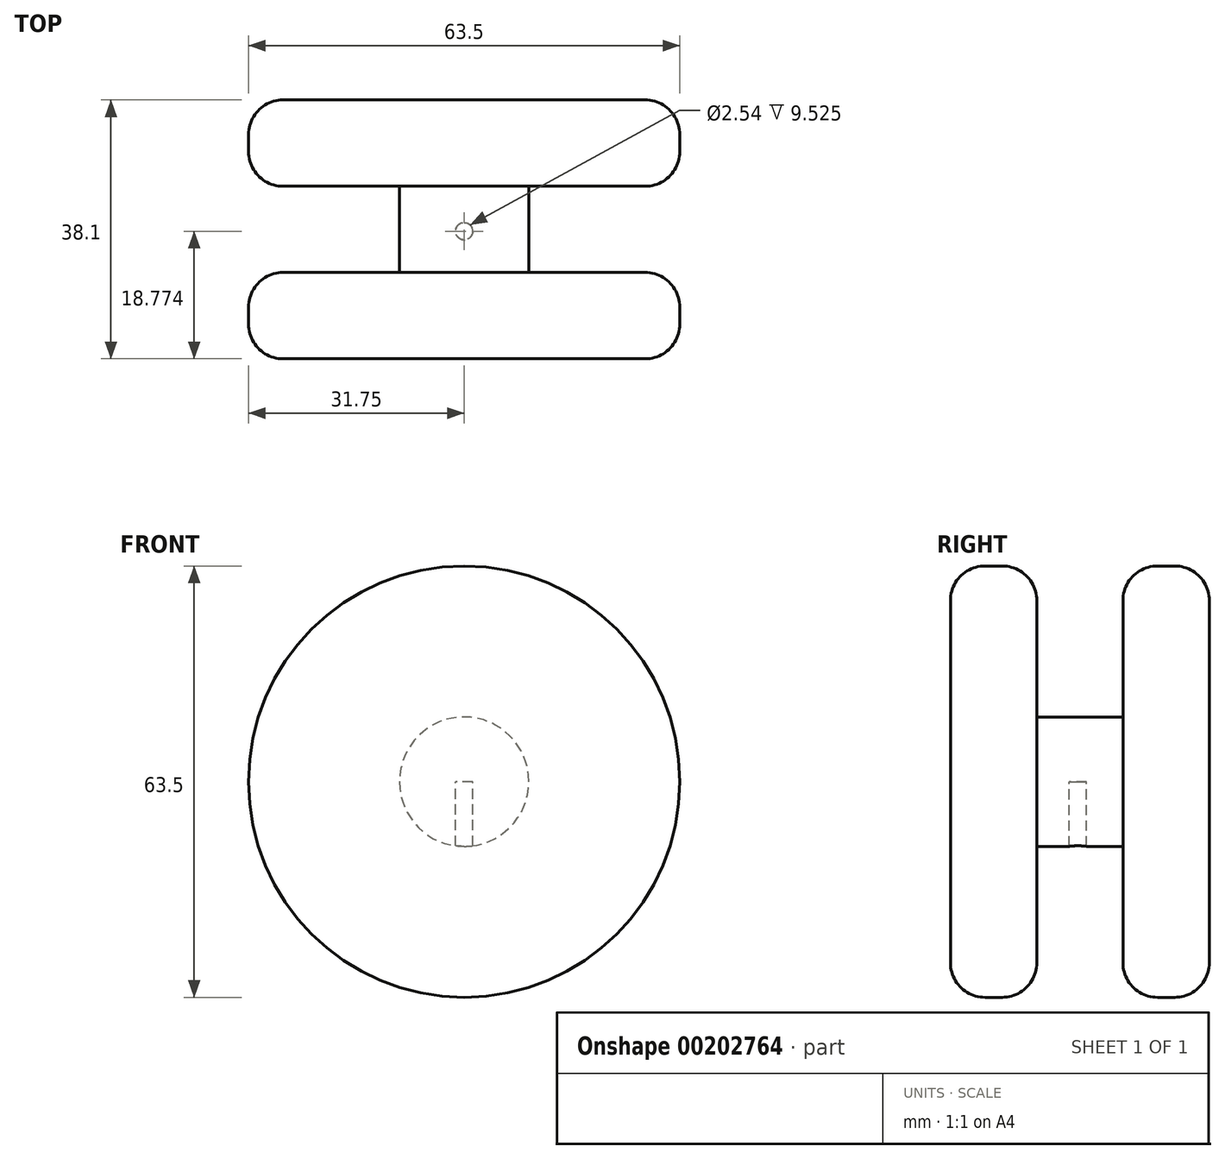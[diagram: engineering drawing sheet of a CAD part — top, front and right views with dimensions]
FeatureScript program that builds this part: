
annotation { "Feature Type Name" : "Feature", "Feature Type Description" : "" }
export const myFeature = defineFeature(function(context is Context, id is Id, definition is map)
    precondition{}
    {
        {
            var Q0;
            Q0=qCreatedBy(makeId("Front.planeOp"),FACE);
            var sketch = newSketch(context, id + "F0", { "sketchPlane" : qUnion([Q0])});
            skCircle(sketch, "E0", {"center": v(0, 0) * mm, "radius": 31.75 * mm});
            skSolve(sketch);
        }
        {
            var Q0;
            Q0=makeQuery(id+"F0.imprint","IMPRINT",FACE,{"disambiguationData":[TD([[makeQuery(id+"F0.imprint","IMPRINT",EDGE,{"derivedFrom":sQuery(id+"F0.wireOp",EDGE,"E0")}),1.0]])]});
            extrude(context, id + "F1", {"entities" : qUnion([Q0]), "depth" : 12.7 * mm});
        }
        {
            var Q0;
            Q0=makeQuery(id+"F1.opExtrude","CAP_FACE",FACE,{"disambiguationData":[OSD([sQuery(id+"F0.wireOp",EDGE,"E0")])],"isStart":false});
            var Q1;
            Q1=makeQuery(id+"F1.opExtrude","CAP_FACE",FACE,{"disambiguationData":[OSD([sQuery(id+"F0.wireOp",EDGE,"E0")])],"isStart":true});
            fillet(context, id + "F2", {"entities" : qUnion([Q0, Q1]), "radius" : 5.08 * mm, "tangentPropagation" : true, "allowEdgeOverflow" : false});
        }
        {
            var Q0;
            Q0=makeQuery(id+"F1.opExtrude","CAP_FACE",FACE,{"disambiguationData":[OSD([sQuery(id+"F0.wireOp",EDGE,"E0")])],"isStart":true});
            var sketch = newSketch(context, id + "F3", { "sketchPlane" : qUnion([Q0])});
            skCircle(sketch, "E1", {"center": v(0, 0) * mm, "radius": 9.53 * mm});
            skSolve(sketch);
        }
        {
            var Q0;
            Q0=makeQuery(id+"F3.imprint","IMPRINT",FACE,{"disambiguationData":[TD([[makeQuery(id+"F3.imprint","IMPRINT",EDGE,{"derivedFrom":sQuery(id+"F3.wireOp",EDGE,"E1")}),1.0]])]});
            extrude(context, id + "F4", {"entities" : qUnion([Q0]), "operationType" : NewBodyOperationType.ADD, "depth" : 6.35 * mm});
        }
        {
            var Q0;
            Q0=makeQuery(id+"F1.opExtrude","SWEPT_BODY",BODY,{"disambiguationData":[OSD([sQuery(id+"F0.wireOp",EDGE,"E0")])]});
            var Q1;
            Q1=makeQuery(id+"F4.opExtrude","CAP_FACE",FACE,{"disambiguationData":[OSD([sQuery(id+"F3.wireOp",EDGE,"E1")])],"isStart":false});
            mirror(context, id + "F5", {"operationType" : NewBodyOperationType.ADD, "entities" : qUnion([Q0]), "mirrorPlane" : qUnion([Q1])});
        }
        {
            var Q0;
            Q0=qCreatedBy(makeId("Top.planeOp"),FACE);
            var sketch = newSketch(context, id + "F6", { "sketchPlane" : qUnion([Q0])});
            skPoint(sketch, "E2", {"position": v(0, 6.07) * mm});
            skSolve(sketch);
        }
        {
            var Q0;
            Q0=sQuery(id+"F6.wireOp",VERTEX,"E2");
            var Q1;
            Q1=makeQuery(id+"F1.opExtrude","SWEPT_BODY",BODY,{"disambiguationData":[OSD([sQuery(id+"F0.wireOp",EDGE,"E0")])]});
            hole(context, id + "F7", {"style" : HoleStyle.SIMPLE, "endStyle" : HoleEndStyle.BLIND, "holeDiameter" : 2.54 * mm, "holeDepth" : 25.4 * mm, "locations" : qUnion([Q0]), "scope" : qUnion([Q1])});
        }
    });
